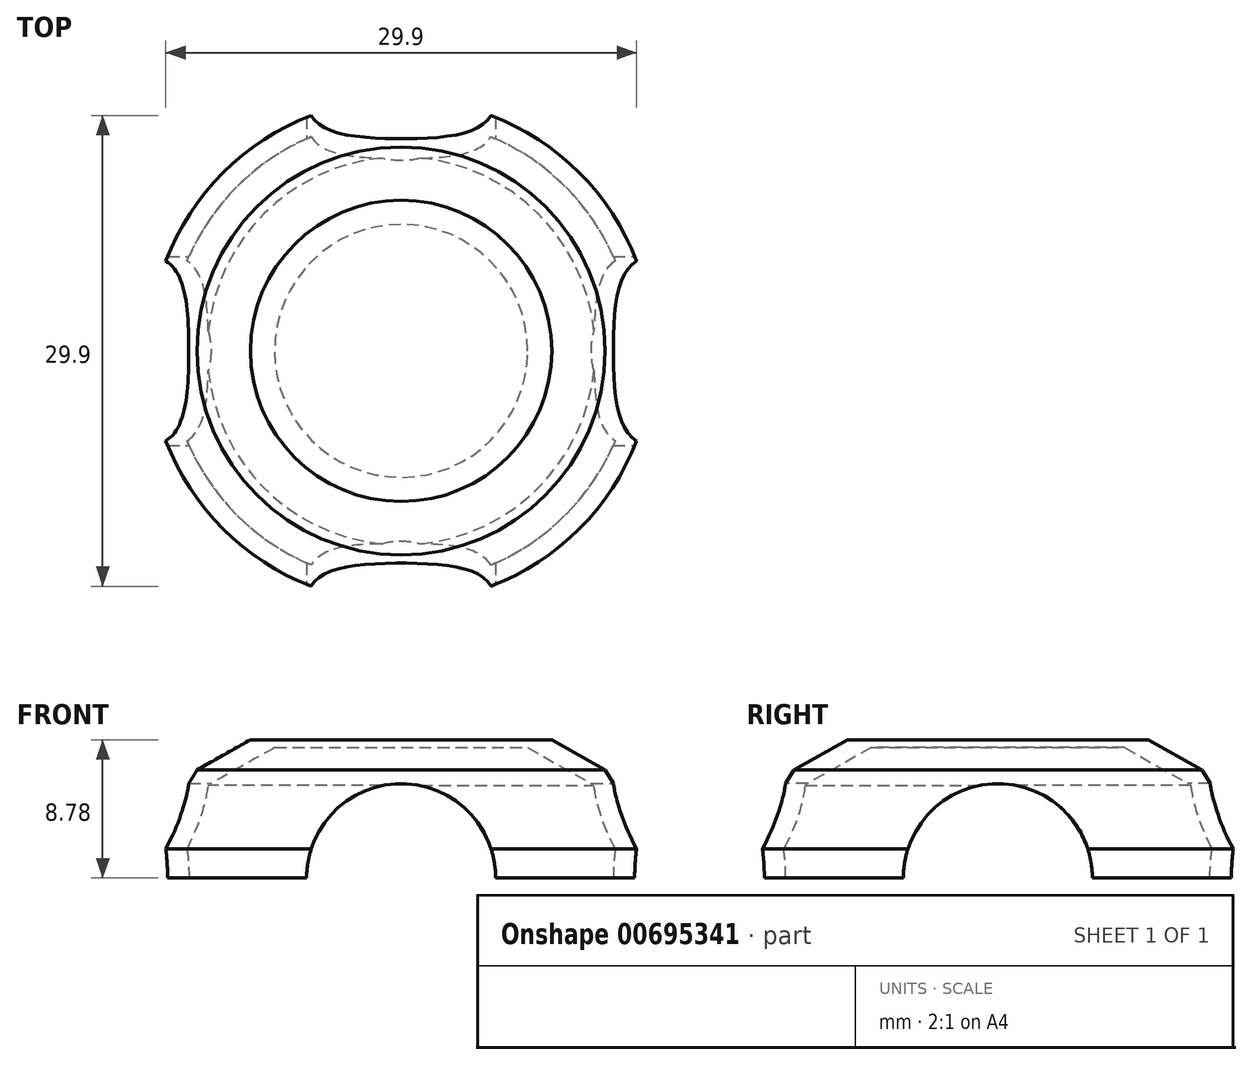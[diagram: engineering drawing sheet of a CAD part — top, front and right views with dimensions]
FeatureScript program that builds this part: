
annotation { "Feature Type Name" : "Feature", "Feature Type Description" : "" }
export const myFeature = defineFeature(function(context is Context, id is Id, definition is map)
    precondition{}
    {
        {
            var Q0;
            Q0=qCreatedBy(makeId("Front.planeOp"),FACE);
            var sketch = newSketch(context, id + "F0", { "sketchPlane" : qUnion([Q0])});
            skLineSegment(sketch, "E0", {"start": v(0, 0) * mm, "end": v(16, 0) * mm});
            skLineSegment(sketch, "E1", {"start": v(0, 0.78) * mm, "end": v(0, 8.78) * mm});
            skLineSegment(sketch, "E2", {"start": v(16, 1.84) * mm, "end": v(12.96, 6.87) * mm});
            skLineSegment(sketch, "E3", {"start": v(16, 0) * mm, "end": v(16, 1.84) * mm});
            skLineSegment(sketch, "E4", {"start": v(16, 0) * mm, "end": v(14.75, 0) * mm});
            skLineSegment(sketch, "E5", {"start": v(14.75, 0) * mm, "end": v(14.75, 1.84) * mm});
            skLineSegment(sketch, "E6", {"start": v(0, 9.28) * mm, "end": v(0, 8.28) * mm});
            skLineSegment(sketch, "E7", {"start": v(0, 8.28) * mm, "end": v(8.04, 8.28) * mm});
            skLineSegment(sketch, "E8", {"start": v(14.75, 1.84) * mm, "end": v(12.31, 5.87) * mm});
            skPoint(sketch, "E9.visualSharp", {"position": v(10.85, 8.28) * mm});
            skPoint(sketch, "E10.visualSharp", {"position": v(11.5, 9.28) * mm});
            skLineSegment(sketch, "E11", {"start": v(9.57, 8.78) * mm, "end": v(12.96, 6.87) * mm});
            skLineSegment(sketch, "E12", {"start": v(8.04, 8.28) * mm, "end": v(12.31, 5.87) * mm});
            skLineSegment(sketch, "E13", {"start": v(0, 8.78) * mm, "end": v(9.57, 8.78) * mm});
            skPoint(sketch, "E13.startSnap0", {"position": v(0, 8.78) * mm});
            skPoint(sketch, "E14.orphan", {"position": v(-0.19, 8.78) * mm});
            skSolve(sketch);
        }
        {
            var Q0;
            Q0=makeQuery(id+"F0.imprint","IMPRINT",FACE,{"disambiguationData":[TD([[makeQuery(id+"F0.imprint","IMPRINT",EDGE,{"derivedFrom":sQuery(id+"F0.wireOp",EDGE,"E2")}),1.0]])]});
            var Q1;
            Q1=sQuery(id+"F0.wireOp",EDGE,"E1");
            revolve(context, id + "F1", {"surfaceOperationType" : NewSurfaceOperationType.NEW, "entities" : qUnion([Q0]), "axis" : qUnion([Q1]), "revolveType" : RevolveType.FULL});
        }
        {
            var Q0;
            Q0=qCreatedBy(makeId("Front.planeOp"),FACE);
            var sketch = newSketch(context, id + "F2", { "sketchPlane" : qUnion([Q0])});
            skCircle(sketch, "E15", {"center": v(0, 0) * mm, "radius": 6 * mm});
            skSolve(sketch);
        }
        {
            var Q0;
            Q0 = qSketchRegion(id + "F2", true);
            extrude(context, id + "F3", {"entities" : qUnion([Q0]), "operationType" : NewBodyOperationType.REMOVE, "oppositeDirection" : true, "depth" : 25 * mm, "offsetDistance" : 25 * mm, "hasSecondDirection" : true, "secondDirectionOppositeDirection" : false, "secondDirectionDepth" : 25 * mm});
        }
        {
            var Q0;
            Q0=qCreatedBy(makeId("Right.planeOp"),FACE);
            var sketch = newSketch(context, id + "F4", { "sketchPlane" : qUnion([Q0])});
            skCircle(sketch, "E16", {"center": v(0, 0) * mm, "radius": 6 * mm});
            skSolve(sketch);
        }
        {
            var Q0;
            Q0=makeQuery(id+"F4.imprint","IMPRINT",FACE,{"disambiguationData":[TD([[makeQuery(id+"F4.imprint","IMPRINT",EDGE,{"derivedFrom":sQuery(id+"F4.wireOp",EDGE,"E16")}),1.0]])]});
            extrude(context, id + "F5", {"entities" : qUnion([Q0]), "operationType" : NewBodyOperationType.REMOVE, "oppositeDirection" : true, "depth" : 25 * mm, "offsetDistance" : 25 * mm, "hasSecondDirection" : true, "secondDirectionOppositeDirection" : false, "secondDirectionDepth" : 25 * mm});
        }
    });
